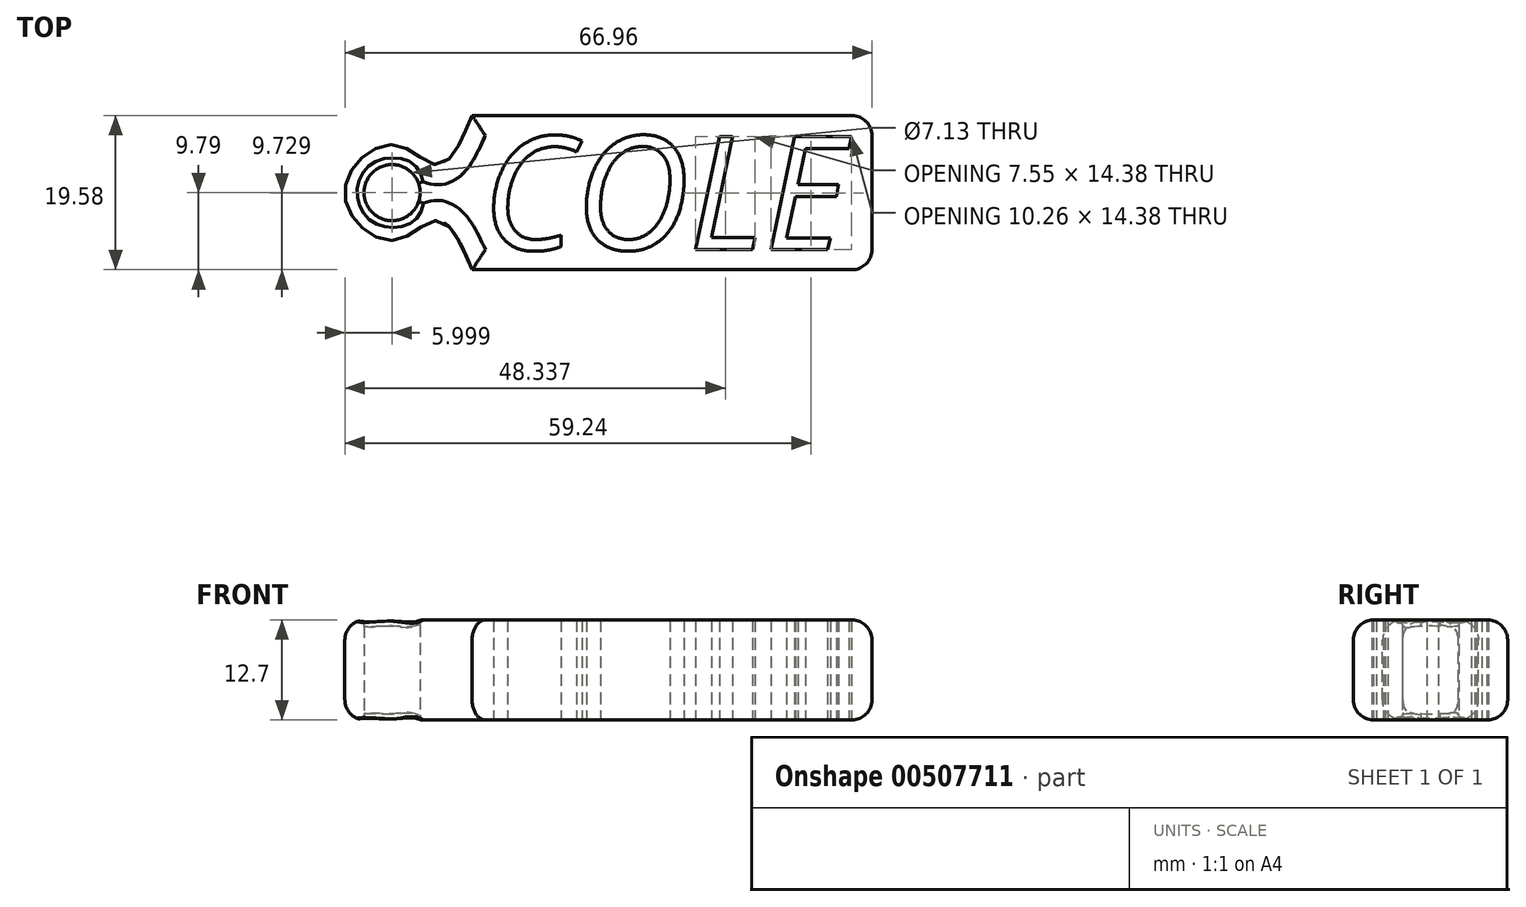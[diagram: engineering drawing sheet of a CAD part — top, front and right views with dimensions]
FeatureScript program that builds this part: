
annotation { "Feature Type Name" : "Feature", "Feature Type Description" : "" }
export const myFeature = defineFeature(function(context is Context, id is Id, definition is map)
    precondition{}
    {
        {
            var Q0;
            Q0=qCreatedBy(makeId("Top.planeOp"),FACE);
            var sketch = newSketch(context, id + "F0", { "sketchPlane" : qUnion([Q0])});
            skLineSegment(sketch, "E0.bottom", {"start": v(-27.95, 9.41) * mm, "end": v(20.3, 9.41) * mm});
            skLineSegment(sketch, "E0.top", {"start": v(-27.95, -10.17) * mm, "end": v(20.3, -10.17) * mm});
            skLineSegment(sketch, "E0.left", {"start": v(-27.95, 9.41) * mm, "end": v(-27.95, -10.17) * mm});
            skLineSegment(sketch, "E0.right", {"start": v(22.85, 6.87) * mm, "end": v(22.85, -7.63) * mm});
            skText(sketch, "E1", { "text": "COLE ", "fontName": "OpenSans-Italic.ttf"});
            skPoint(sketch, "E2.3.internal.snap0", {"position": v(-26.68, -0.38) * mm});
            skFitSpline(sketch, "E2", {"points": [v(-27.95, -10.17) * mm, v(-32.3, -3.91) * mm, v(-38.11, -6.46) * mm, v(-44.11, -0.38) * mm, v(-38.11, 5.7) * mm, v(-32.3, 3.15) * mm, v(-27.95, 9.41) * mm], "startDerivative": vector(-20.18, 49.76) * mm, "endDerivative": vector(24.62, 58.52) * mm});
            skCircle(sketch, "E3", {"center": v(-38.11, -0.38) * mm, "radius": 3.56 * mm});
            skPoint(sketch, "E4.visualSharp", {"position": v(22.85, 9.41) * mm});
            skArc(sketch, "E4.filletArc", {"start": v(22.85, 6.87) * mm, "mid": v(22.1, 8.67) * mm, "end": v(20.3, 9.41) * mm});
            skPoint(sketch, "E5.visualSharp", {"position": v(22.85, -10.17) * mm});
            skArc(sketch, "E5.filletArc", {"start": v(20.3, -10.17) * mm, "mid": v(22.1, -9.43) * mm, "end": v(22.85, -7.63) * mm});
            const initialGuessF0  = {"E1": [-0.02668, -0.00763, 1, 0, 0.0145]};
            skSetInitialGuess(sketch, initialGuessF0);
            skSolve(sketch);
        }
        {
            var Q0;
            Q0=makeQuery(id+"F0.imprint","IMPRINT",FACE,{"disambiguationData":[TD([[makeQuery(id+"F0.imprint","IMPRINT",EDGE,{"derivedFrom":sQuery(id+"F0.wireOp",EDGE,"E0.bottom")}),-1.0]])]});
            var Q1;
            Q1=makeQuery(id+"F0.imprint","IMPRINT",FACE,{"disambiguationData":[TD([[makeQuery(id+"F0.imprint","IMPRINT",EDGE,{"derivedFrom":sQuery(id+"F0.wireOp",EDGE,"E1.sketch_text.stroke-27")}),1.0]])]});
            extrude(context, id + "F1", {"entities" : qUnion([Q0, Q1]), "depth" : 12.7 * mm});
        }
        {
            var Q0;
            Q0=makeQuery(id+"F0.imprint","IMPRINT",FACE,{"disambiguationData":[TD([[makeQuery(id+"F0.imprint","IMPRINT",EDGE,{"derivedFrom":sQuery(id+"F0.wireOp",EDGE,"E0.left")}),-1.0]])]});
            extrude(context, id + "F2", {"entities" : qUnion([Q0]), "operationType" : NewBodyOperationType.ADD, "depth" : 12.7 * mm});
        }
        {
            var Q0;
            Q0=makeQuery(id+"F1.opExtrude","CAP_EDGE",EDGE,{"disambiguationData":[OSD([sQuery(id+"F0.wireOp",EDGE,"E0.right")])],"isStart":false});
            var Q1;
            Q1=makeQuery(id+"F1.opExtrude","CAP_EDGE",EDGE,{"disambiguationData":[OSD([sQuery(id+"F0.wireOp",EDGE,"E0.right")])],"isStart":true});
            var Q2;
            Q2=makeQuery(id+"F2.opExtrude","CAP_EDGE",EDGE,{"disambiguationData":[OSD([sQuery(id+"F0.wireOp",EDGE,"E2")])],"isStart":false});
            var Q3;
            Q3=makeQuery(id+"F2.opExtrude","CAP_EDGE",EDGE,{"disambiguationData":[OSD([sQuery(id+"F0.wireOp",EDGE,"E2")])],"isStart":true});
            fillet(context, id + "F3", {"entities" : qUnion([Q0, Q1, Q2, Q3]), "radius" : 2.54 * mm, "tangentPropagation" : true, "allowEdgeOverflow" : false});
        }
        {
            var Q0;
            Q0=makeQuery(id+"F2.opExtrude","SWEPT_FACE",FACE,{"disambiguationData":[OSD([sQuery(id+"F0.wireOp",EDGE,"E3")])]});
            var Q1;
            Q1=makeQuery(id+"F2.opExtrude","CAP_EDGE",EDGE,{"disambiguationData":[OSD([sQuery(id+"F0.wireOp",EDGE,"E3")])],"isStart":false});
            fillet(context, id + "F4", {"entities" : qUnion([Q0, Q1]), "radius" : 0.64 * mm, "tangentPropagation" : true, "allowEdgeOverflow" : false});
        }
    });
